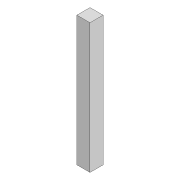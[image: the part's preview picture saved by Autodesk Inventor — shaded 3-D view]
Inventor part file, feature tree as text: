
AUTODESK INVENTOR PART (.ipt)
format: ipt  version: 2022 (Build 260153000, 153)  size: 74,752 bytes
history: native  units: mm
features: extrude x1, sketch x1
ambient origin geometry x8: Origin, YZ Plane, XZ Plane, XY Plane, X Axis, Y Axis, Z Axis, Center Point
bodies: Solid1 (feature_tree)
feature tree (2):
  extrude  "Extrusion1"  Depth=20.2mm
  sketch  "Sketch1"  dims[d0=20.2mm d1=20.2mm d2=200.0mm d3=0.0mm]
